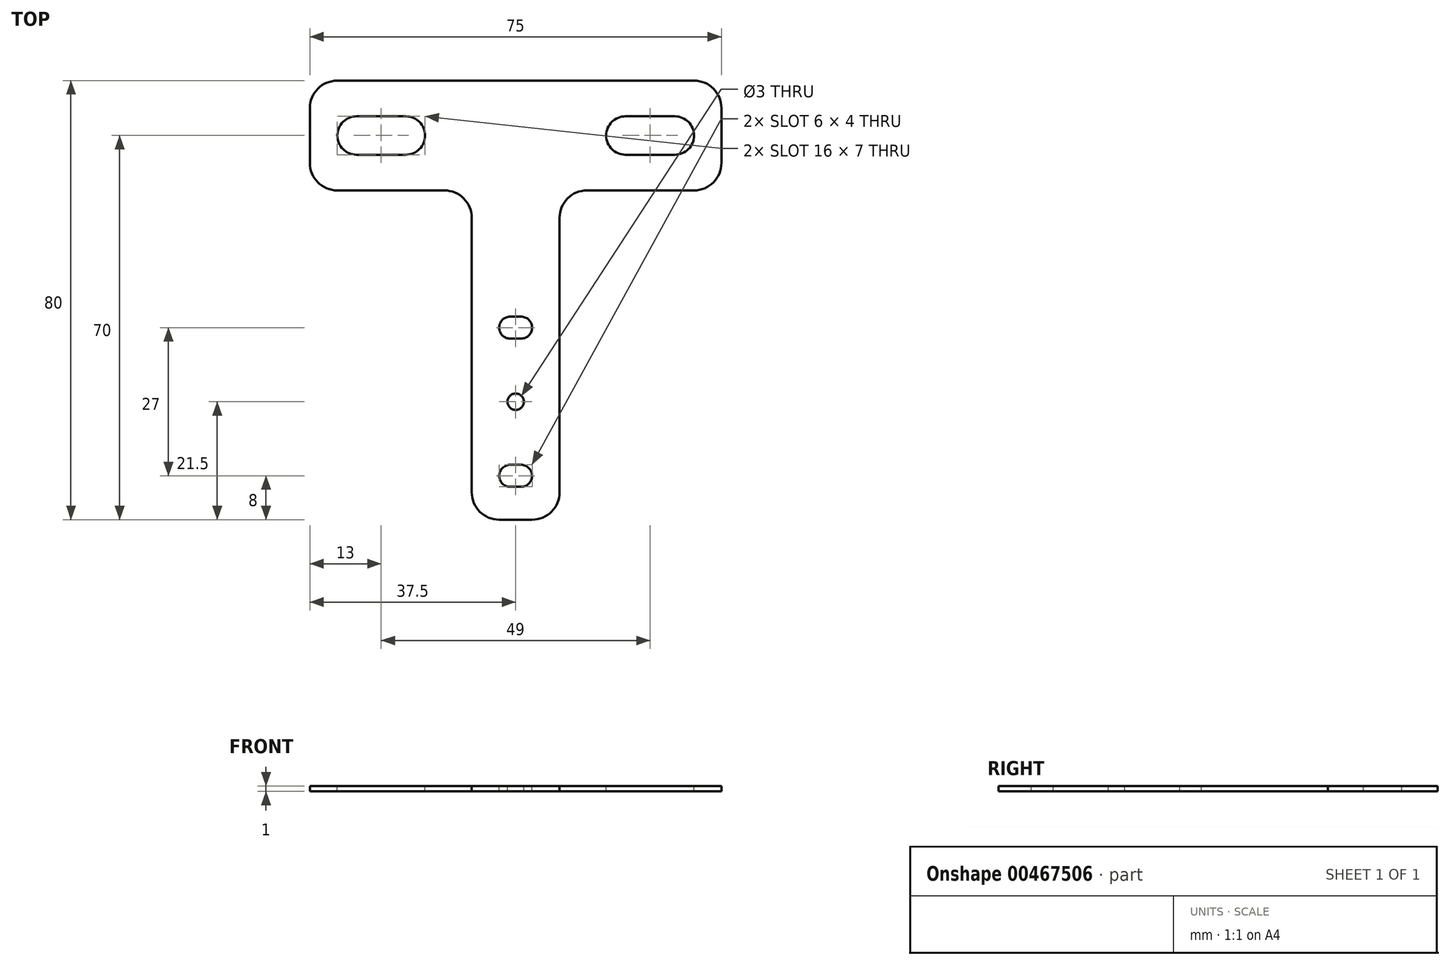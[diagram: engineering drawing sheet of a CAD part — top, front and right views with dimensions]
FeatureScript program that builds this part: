
annotation { "Feature Type Name" : "Feature", "Feature Type Description" : "" }
export const myFeature = defineFeature(function(context is Context, id is Id, definition is map)
    precondition{}
    {
        {
            var Q0;
            Q0=qCreatedBy(makeId("Top.planeOp"),FACE);
            var sketch = newSketch(context, id + "F0", { "sketchPlane" : qUnion([Q0])});
            skLineSegment(sketch, "E0", {"start": v(-32.5, 20) * mm, "end": v(32.5, 20) * mm});
            skLineSegment(sketch, "E1", {"start": v(37.5, 15) * mm, "end": v(37.5, 5) * mm});
            skLineSegment(sketch, "E2", {"start": v(32.5, 0) * mm, "end": v(13, 0) * mm});
            skLineSegment(sketch, "E3", {"start": v(8, -5) * mm, "end": v(8, -55) * mm});
            skLineSegment(sketch, "E4", {"start": v(3, -60) * mm, "end": v(-3, -60) * mm});
            skLineSegment(sketch, "E5", {"start": v(-8, -55) * mm, "end": v(-8, -5) * mm});
            skLineSegment(sketch, "E6", {"start": v(-13, 0) * mm, "end": v(-32.5, 0) * mm});
            skLineSegment(sketch, "E7", {"start": v(-37.5, 5) * mm, "end": v(-37.5, 15) * mm});
            skPoint(sketch, "E8.visualSharp", {"position": v(-37.5, 20) * mm});
            skArc(sketch, "E8.filletArc", {"start": v(-32.5, 20) * mm, "mid": v(-36.04, 18.54) * mm, "end": v(-37.5, 15) * mm});
            skPoint(sketch, "E9.visualSharp", {"position": v(-37.5, 0) * mm});
            skArc(sketch, "E9.filletArc", {"start": v(-37.5, 5) * mm, "mid": v(-36.04, 1.46) * mm, "end": v(-32.5, 0) * mm});
            skPoint(sketch, "E10.visualSharp", {"position": v(37.5, 0) * mm});
            skArc(sketch, "E10.filletArc", {"start": v(32.5, 0) * mm, "mid": v(36.04, 1.46) * mm, "end": v(37.5, 5) * mm});
            skPoint(sketch, "E11.visualSharp", {"position": v(37.5, 20) * mm});
            skArc(sketch, "E11.filletArc", {"start": v(37.5, 15) * mm, "mid": v(36.04, 18.54) * mm, "end": v(32.5, 20) * mm});
            skPoint(sketch, "E12.visualSharp", {"position": v(8, -60) * mm});
            skArc(sketch, "E12.filletArc", {"start": v(3, -60) * mm, "mid": v(6.54, -58.54) * mm, "end": v(8, -55) * mm});
            skPoint(sketch, "E13.visualSharp", {"position": v(-8, -60) * mm});
            skArc(sketch, "E13.filletArc", {"start": v(-8, -55) * mm, "mid": v(-6.54, -58.54) * mm, "end": v(-3, -60) * mm});
            skPoint(sketch, "E14.visualSharp", {"position": v(-8, 0) * mm});
            skArc(sketch, "E14.filletArc", {"start": v(-8, -5) * mm, "mid": v(-9.46, -1.46) * mm, "end": v(-13, 0) * mm});
            skPoint(sketch, "E15.visualSharp", {"position": v(8, 0) * mm});
            skArc(sketch, "E15.filletArc", {"start": v(13, 0) * mm, "mid": v(9.46, -1.46) * mm, "end": v(8, -5) * mm});
            skSolve(sketch);
        }
        {
            var Q0;
            Q0 = qSketchRegion(id + "F0", true);
            extrude(context, id + "F1", {"entities" : qUnion([Q0]), "depth" : 1 * mm});
        }
        {
            var Q0;
            Q0=makeQuery(id+"F1.opExtrude","CAP_FACE",FACE,{"disambiguationData":[OSD([sQuery(id+"F0.wireOp",EDGE,"E0"),sQuery(id+"F0.wireOp",EDGE,"E1"),sQuery(id+"F0.wireOp",EDGE,"E2"),sQuery(id+"F0.wireOp",EDGE,"E3"),sQuery(id+"F0.wireOp",EDGE,"E4"),sQuery(id+"F0.wireOp",EDGE,"E5"),sQuery(id+"F0.wireOp",EDGE,"E6"),sQuery(id+"F0.wireOp",EDGE,"E7"),sQuery(id+"F0.wireOp",EDGE,"E8.filletArc"),sQuery(id+"F0.wireOp",EDGE,"E9.filletArc"),sQuery(id+"F0.wireOp",EDGE,"E10.filletArc"),sQuery(id+"F0.wireOp",EDGE,"E11.filletArc"),sQuery(id+"F0.wireOp",EDGE,"E12.filletArc"),sQuery(id+"F0.wireOp",EDGE,"E13.filletArc"),sQuery(id+"F0.wireOp",EDGE,"E14.filletArc"),sQuery(id+"F0.wireOp",EDGE,"E15.filletArc")])],"isStart":false});
            var sketch = newSketch(context, id + "F2", { "sketchPlane" : qUnion([Q0])});
            skLineSegment(sketch, "E16.bottom", {"start": v(-1, -50) * mm, "end": v(1, -50) * mm});
            skLineSegment(sketch, "E16.top", {"start": v(-1, -54) * mm, "end": v(1, -54) * mm});
            skLineSegment(sketch, "E17.bottom", {"start": v(-1, -23) * mm, "end": v(1, -23) * mm});
            skLineSegment(sketch, "E17.top", {"start": v(-1, -27) * mm, "end": v(1, -27) * mm});
            skLineSegment(sketch, "E18.bottom", {"start": v(20, 13.5) * mm, "end": v(29, 13.5) * mm});
            skLineSegment(sketch, "E18.top", {"start": v(20, 6.5) * mm, "end": v(29, 6.5) * mm});
            skLineSegment(sketch, "E19.bottom", {"start": v(-29, 13.5) * mm, "end": v(-20, 13.5) * mm});
            skLineSegment(sketch, "E19.top", {"start": v(-29, 6.5) * mm, "end": v(-20, 6.5) * mm});
            skCircle(sketch, "E20", {"center": v(0, -38.5) * mm, "radius": 1.5 * mm});
            skArc(sketch, "E21", {"start": v(-1, -23) * mm, "mid": v(-3, -25) * mm, "end": v(-1, -27) * mm});
            skArc(sketch, "E22", {"start": v(1, -27) * mm, "mid": v(3, -25) * mm, "end": v(1, -23) * mm});
            skArc(sketch, "E23", {"start": v(1, -54) * mm, "mid": v(3, -52) * mm, "end": v(1, -50) * mm});
            skArc(sketch, "E24", {"start": v(-1, -50) * mm, "mid": v(-3, -52) * mm, "end": v(-1, -54) * mm});
            skArc(sketch, "E25", {"start": v(-20, 6.5) * mm, "mid": v(-16.5, 10) * mm, "end": v(-20, 13.5) * mm});
            skArc(sketch, "E26", {"start": v(29, 6.5) * mm, "mid": v(32.5, 10) * mm, "end": v(29, 13.5) * mm});
            skArc(sketch, "E27", {"start": v(20, 13.5) * mm, "mid": v(16.5, 10) * mm, "end": v(20, 6.5) * mm});
            skArc(sketch, "E28", {"start": v(-29, 13.5) * mm, "mid": v(-32.5, 10) * mm, "end": v(-29, 6.5) * mm});
            skSolve(sketch);
        }
        {
            var Q0;
            Q0 = qSketchRegion(id + "F2", true);
            extrude(context, id + "F3", {"entities" : qUnion([Q0]), "operationType" : NewBodyOperationType.REMOVE, "endBound" : BoundingType.THROUGH_ALL, "oppositeDirection" : true, "depth" : 25 * mm});
        }
    });
